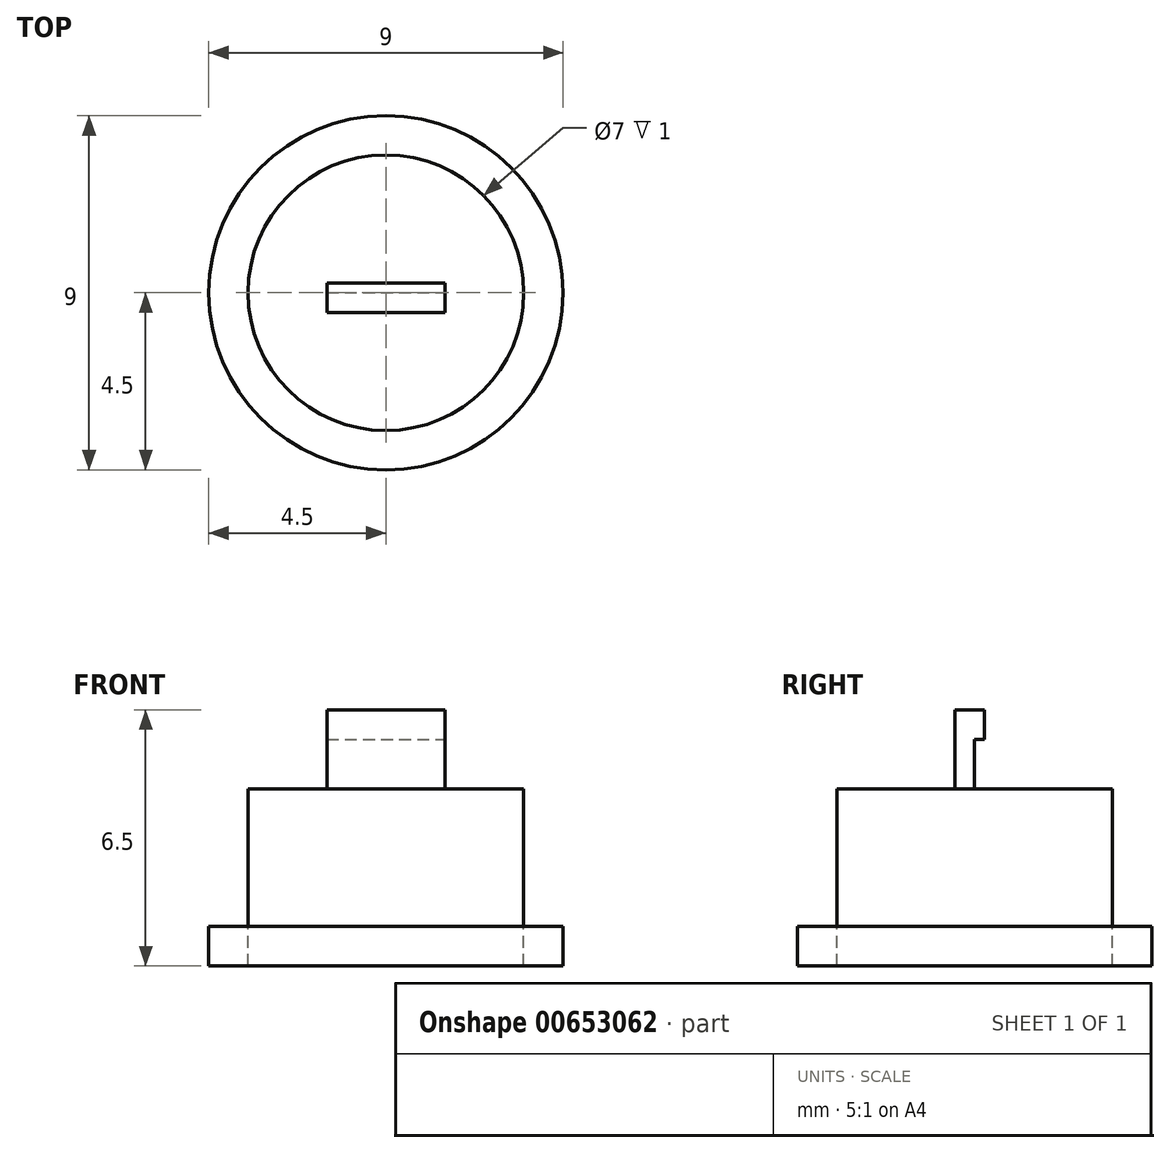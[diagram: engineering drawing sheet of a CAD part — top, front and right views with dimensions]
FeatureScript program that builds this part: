
annotation { "Feature Type Name" : "Feature", "Feature Type Description" : "" }
export const myFeature = defineFeature(function(context is Context, id is Id, definition is map)
    precondition{}
    {
        {
            var Q0;
            Q0=qCreatedBy(makeId("Top.planeOp"),FACE);
            var sketch = newSketch(context, id + "F0", { "sketchPlane" : qUnion([Q0])});
            skCircle(sketch, "E0", {"center": v(0, 0) * mm, "radius": 3.5 * mm});
            skSolve(sketch);
        }
        {
            var Q0;
            Q0=makeQuery(id+"F0.imprint","IMPRINT",FACE,{"disambiguationData":[TD([[makeQuery(id+"F0.imprint","IMPRINT",EDGE,{"derivedFrom":sQuery(id+"F0.wireOp",EDGE,"E0")}),1.0]])]});
            extrude(context, id + "F1", {"entities" : qUnion([Q0]), "depth" : 3.5 * mm, "offsetDistance" : 25.4 * mm});
        }
        {
            var Q0;
            Q0=makeQuery(id+"F1.opExtrude","CAP_FACE",FACE,{"disambiguationData":[OSD([sQuery(id+"F0.wireOp",EDGE,"E0")])],"isStart":true});
            var sketch = newSketch(context, id + "F2", { "sketchPlane" : qUnion([Q0])});
            skCircle(sketch, "E1", {"center": v(0, 0) * mm, "radius": 4.5 * mm});
            skSolve(sketch);
        }
        {
            var Q0;
            Q0=makeQuery(id+"F2.imprint","IMPRINT",FACE,{"disambiguationData":[TD([[makeQuery(id+"F2.imprint","IMPRINT",EDGE,{"derivedFrom":sQuery(id+"F2.wireOp",EDGE,"E1")}),1.0]])]});
            extrude(context, id + "F3", {"entities" : qUnion([Q0]), "depth" : 1 * mm, "offsetDistance" : 25.4 * mm});
        }
        {
            var Q0;
            Q0=makeQuery(id+"F1.opExtrude","CAP_FACE",FACE,{"disambiguationData":[OSD([sQuery(id+"F0.wireOp",EDGE,"E0")])],"isStart":true});
            var sketch = newSketch(context, id + "F4", { "sketchPlane" : qUnion([Q0])});
            skCircle(sketch, "E2", {"center": v(0, 0) * mm, "radius": 3.5 * mm});
            skSolve(sketch);
        }
        {
            var Q0;
            Q0=makeQuery(id+"F4.imprint","IMPRINT",FACE,{"disambiguationData":[TD([[makeQuery(id+"F4.imprint","IMPRINT",EDGE,{"derivedFrom":sQuery(id+"F4.wireOp",EDGE,"E2")}),-1.0]])]});
            extrude(context, id + "F5", {"entities" : qUnion([Q0]), "depth" : 1 * mm, "offsetDistance" : 25.4 * mm});
        }
        {
            var Q0;
            Q0=makeQuery(id+"F1.opExtrude","CAP_FACE",FACE,{"disambiguationData":[OSD([sQuery(id+"F0.wireOp",EDGE,"E0")])],"isStart":false});
            var sketch = newSketch(context, id + "F6", { "sketchPlane" : qUnion([Q0])});
            skLineSegment(sketch, "E3.bottom", {"start": v(-1.5, 1.5) * mm, "end": v(1.5, 1.5) * mm});
            skLineSegment(sketch, "E3.top", {"start": v(-1.5, -1.5) * mm, "end": v(1.5, -1.5) * mm});
            skLineSegment(sketch, "E3.left", {"start": v(-1.5, 1.5) * mm, "end": v(-1.5, -1.5) * mm});
            skLineSegment(sketch, "E3.right", {"start": v(1.5, 1.5) * mm, "end": v(1.5, -1.5) * mm});
            skSolve(sketch);
        }
        {
            var Q0;
            Q0=makeQuery(id+"F6.imprint","IMPRINT",FACE,{"disambiguationData":[TD([[makeQuery(id+"F6.imprint","IMPRINT",EDGE,{"derivedFrom":sQuery(id+"F6.wireOp",EDGE,"E3.bottom")}),-1.0]])]});
            extrude(context, id + "F7", {"entities" : qUnion([Q0]), "operationType" : NewBodyOperationType.ADD, "depth" : 2 * mm, "offsetDistance" : 25.4 * mm});
        }
        {
            var Q0;
            Q0=makeQuery(id+"F7.opExtrude","SWEPT_FACE",FACE,{"disambiguationData":[OSD([sQuery(id+"F6.wireOp",EDGE,"E3.right")])]});
            var sketch = newSketch(context, id + "F8", { "sketchPlane" : qUnion([Q0])});
            skPoint(sketch, "E4.endSnap0", {"position": v(0, 5.5) * mm});
            skLineSegment(sketch, "E5.bottom", {"start": v(-0.5, 3.5) * mm, "end": v(0.25, 3.5) * mm});
            skLineSegment(sketch, "E5.top", {"start": v(-0.5, 5.5) * mm, "end": v(0.25, 5.5) * mm});
            skLineSegment(sketch, "E5.left", {"start": v(-0.5, 3.5) * mm, "end": v(-0.5, 5.5) * mm});
            skLineSegment(sketch, "E5.right", {"start": v(0.25, 3.5) * mm, "end": v(0.25, 5.5) * mm});
            skLineSegment(sketch, "E6", {"start": v(0, 5.5) * mm, "end": v(0, 3.5) * mm});
            skLineSegment(sketch, "E7", {"start": v(0, 5.5) * mm, "end": v(0, 4.75) * mm});
            skLineSegment(sketch, "E8", {"start": v(0, 4.75) * mm, "end": v(0.25, 4.75) * mm});
            skLineSegment(sketch, "E9", {"start": v(0.25, 4.75) * mm, "end": v(-0.5, 5.5) * mm});
            skLineSegment(sketch, "E10", {"start": v(0, 4.75) * mm, "end": v(0, 3.5) * mm});
            skPoint(sketch, "E11", {"position": v(-0.5, 4.75) * mm});
            skSolve(sketch);
        }
        {
            var Q0;
            {var subQ4=sQuery(id+"F8.wireOp",EDGE,"E8");Q0=makeQuery(id+"F8.imprint","IMPRINT",FACE,{"disambiguationData":[TD([[makeQuery(id+"F8.imprint","IMPRINT",EDGE,{"derivedFrom":subQ4}),-1.0]])]});}
            var Q1;
            {var subQ1=sQuery(id+"F8.wireOp",EDGE,"E5.top");var subQ3=sQuery(id+"F8.wireOp",EDGE,"E7");var subQ4=makeQuery(id+"F8.imprint","INTERSECT",VERTEX,{"derivedFrom":[subQ1,subQ3]});Q1=makeQuery(id+"F8.imprint","IMPRINT",FACE,{"disambiguationData":[TD([[makeQuery(id+"F8.imprint","IMPRINT",EDGE,{"disambiguationData":[TD([[subQ4,-1.0]])],"derivedFrom":subQ3}),1.0]])]});}
            var Q2;
            {var subQ1=sQuery(id+"F8.wireOp",EDGE,"E5.top");var subQ3=sQuery(id+"F8.wireOp",EDGE,"E7");var subQ4=makeQuery(id+"F8.imprint","INTERSECT",VERTEX,{"derivedFrom":[subQ1,subQ3]});Q2=makeQuery(id+"F8.imprint","IMPRINT",FACE,{"disambiguationData":[TD([[makeQuery(id+"F8.imprint","IMPRINT",EDGE,{"disambiguationData":[TD([[subQ4,-1.0]])],"derivedFrom":subQ3}),-1.0]])]});}
            var Q3;
            {var subQ0=sQuery(id+"F8.wireOp",EDGE,"E5.left");Q3=makeQuery(id+"F8.imprint","IMPRINT",FACE,{"disambiguationData":[TD([[makeQuery(id+"F8.imprint","IMPRINT",EDGE,{"derivedFrom":subQ0}),1.0]])]});}
            var Q4;
            {var subQ0=sQuery(id+"F6.wireOp",EDGE,"E3.right");var subQ1=makeQuery(id+"F7.opExtrude","SWEPT_EDGE",EDGE,{"disambiguationData":[OSD([sQuery(id+"F6.wireOp",EDGE,"E3.bottom"),subQ0])]});Q4=makeQuery(id+"F8.imprint","IMPRINT",FACE,{"disambiguationData":[TD([[makeQuery(id+"F8.imprint","IMPRINT",EDGE,{"derivedFrom":subQ1}),-1.0]])]});}
            extrude(context, id + "F9", {"entities" : qUnion([Q0, Q1, Q2, Q3, Q4]), "operationType" : NewBodyOperationType.REMOVE, "oppositeDirection" : true, "depth" : 25.4 * mm, "offsetDistance" : 25.4 * mm});
        }
    });
